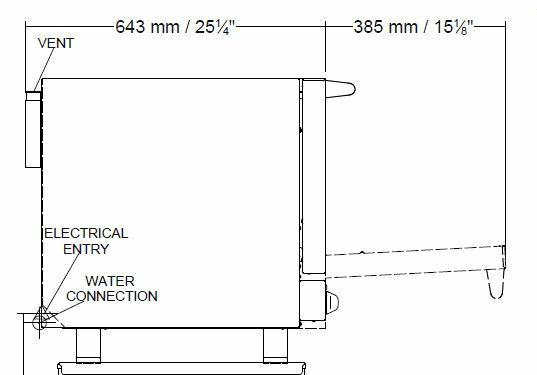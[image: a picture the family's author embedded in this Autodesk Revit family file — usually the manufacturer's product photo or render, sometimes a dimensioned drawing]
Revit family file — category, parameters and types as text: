
# Revit family: QF_MOFFAT_E28D4_NZ
name_source: partatom
category: Specialty Equipment
revit_build: Autodesk Revit 2014 (Build: 20130308_1515(x64)
units: mm (PartAtom-declared; Revit-internal decimal feet)

## types (1)
- QF_MOFFAT_E28D4_NZ
    Apparent Power = 5750 VA
    Cold Water Connection Height = 0 mm  [stored 0 ft]
    Cold Water Flow = 0 GPM
    Cold Water Maximum Pressure = 80.00 psi
    Cold Water Minimum Pressure = 20.00 psi
    Cold Water RI Height = 0 mm  [stored 0 ft]
    Cold Water Size = 1"
    Cold Water Temperature Recommended = 0 °F
    Conn Conduit = Yes
    Depth = 762 mm  [stored 2.5 ft]
    Description = FULL SIZE DIGITAL / ELECTRIC CONVECTION OVEN ON A STAINLESS STEEL STAND
    Elec Conn Connection Height = 0 mm  [stored 0 ft]
    Elec Conn RI Height = 0 mm  [stored 0 ft]
    Electrical Remarks = 230-240V, 50/60Hz, 1P+N+E, 5.8kW, 25A
    Exhaust RI Height = 0 mm  [stored 0 ft]
    Exhaust Static Press = 0.00 in-wg
    Exhaust Vent Depth = 0 mm  [stored 0 ft]
    Exhaust Vent Diameter = 0 mm  [stored 0 ft]
    Exhaust Vent Width = 0 mm  [stored 0 ft]
    Exhaust Volume = 0 CFM
    FL Amps = 25 A
    Foodservice Equipment Identifier = Yes
    Height = 1542 mm  [stored 5.05906 ft]
    Height of Stand = 880 mm  [stored 2.88714 ft]
    Identify Quantity as Lot = Yes
    Length = 810 mm
    Manufacturer = MOFFAT
    Max Overcurrent Protection = 0 A
    Min Ckt Ampacity = 0 A
    Model = E28D4
    Number of Poles = 1
    Phase = 1
    URL = www.moffat.com.au
    URL Cutsheet = www.moffat.com.au
    Volts = 230 V
    Watts = 5800 W
    Weight in Pounds = 0

note: [stored X ft] marks values corroborated as IEEE doubles in the binary element streams (Revit-internal decimal feet)

## geometry (parser evidence)
native form markers: Blend x12, Sweep x9
no freeform markers — native parametric forms only
